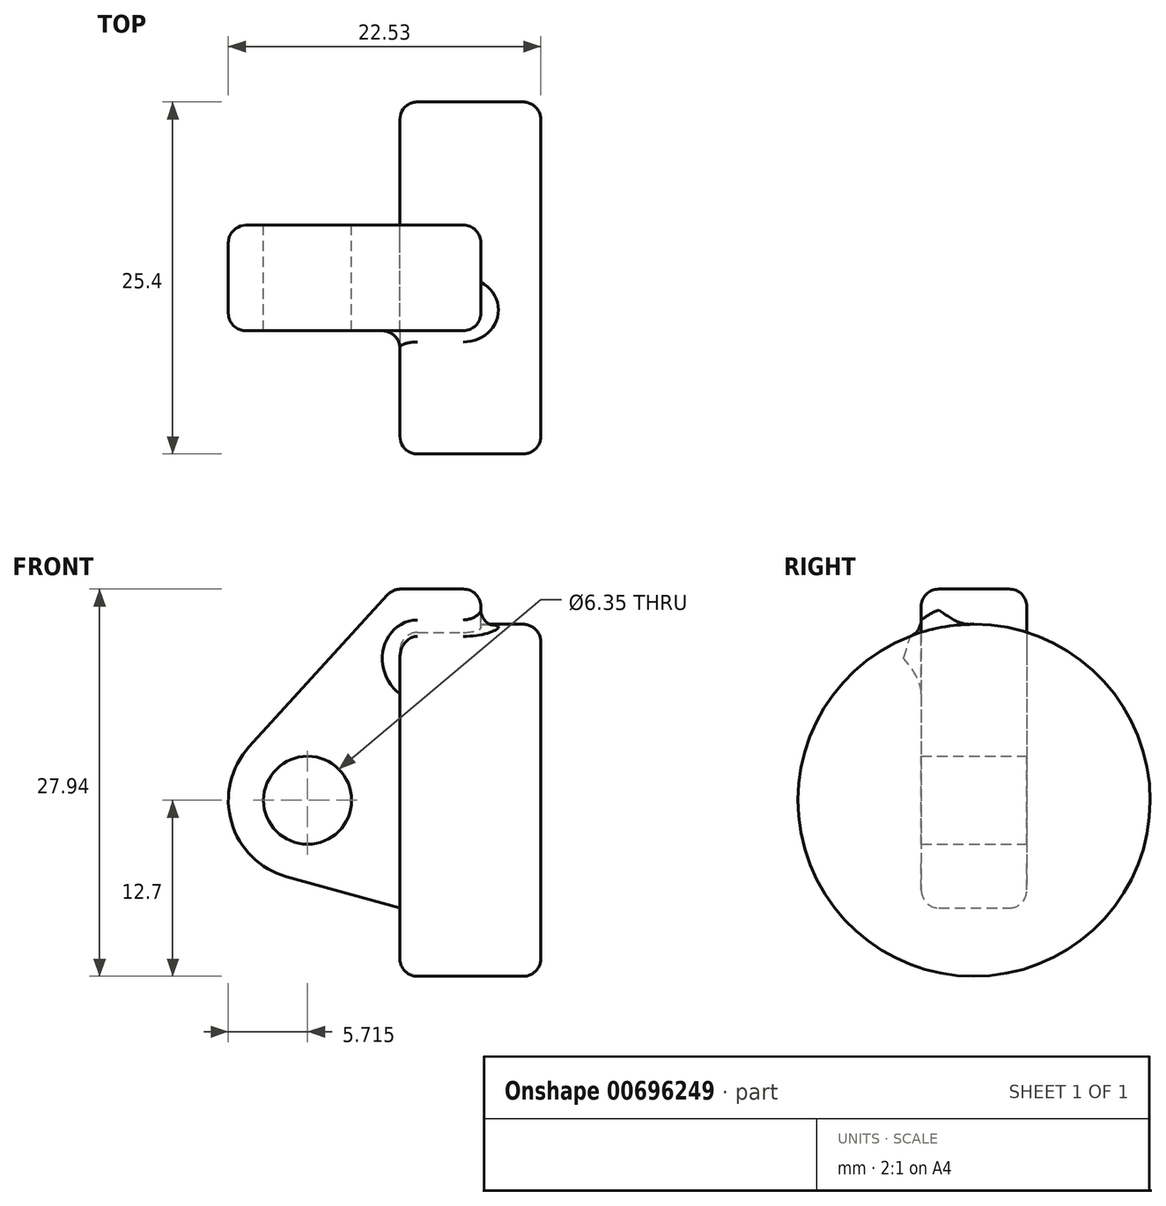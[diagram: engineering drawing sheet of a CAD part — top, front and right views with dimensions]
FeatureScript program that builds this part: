
annotation { "Feature Type Name" : "Feature", "Feature Type Description" : "" }
export const myFeature = defineFeature(function(context is Context, id is Id, definition is map)
    precondition{}
    {
        {
            var Q0;
            Q0=qCreatedBy(makeId("Front.planeOp"),FACE);
            var sketch = newSketch(context, id + "F0", { "sketchPlane" : qUnion([Q0])});
            skLineSegment(sketch, "E0", {"start": v(0, 0) * mm, "end": v(0, 12.7) * mm});
            skLineSegment(sketch, "E1", {"start": v(0, 12.7) * mm, "end": v(10.16, 12.7) * mm});
            skLineSegment(sketch, "E2", {"start": v(10.16, 12.7) * mm, "end": v(10.16, 10.16) * mm});
            skLineSegment(sketch, "E3", {"start": v(10.16, 10.16) * mm, "end": v(56.13, 10.16) * mm});
            skLineSegment(sketch, "E4", {"start": v(56.13, 10.16) * mm, "end": v(56.13, 12.7) * mm});
            skLineSegment(sketch, "E5", {"start": v(56.13, 12.7) * mm, "end": v(66.3, 12.7) * mm});
            skLineSegment(sketch, "E6", {"start": v(66.3, 12.7) * mm, "end": v(66.3, 0) * mm});
            skLineSegment(sketch, "E7", {"start": v(66.3, 0) * mm, "end": v(0, 0) * mm});
            skLineSegment(sketch, "E8", {"start": v(5.84, 15.24) * mm, "end": v(-0.5, 15.24) * mm});
            skLineSegment(sketch, "E9", {"start": v(-0.5, 15.24) * mm, "end": v(-10.88, 3.85) * mm});
            skLineSegment(sketch, "E10", {"start": v(0, 0) * mm, "end": v(-6.65, 0) * mm});
            skCircle(sketch, "E11", {"center": v(-6.65, 0) * mm, "radius": 5.72 * mm});
            skCircle(sketch, "E12", {"center": v(-6.65, 0) * mm, "radius": 3.18 * mm});
            skLineSegment(sketch, "E13", {"start": v(5.84, 15.24) * mm, "end": v(5.84, -9.4) * mm});
            skLineSegment(sketch, "E14", {"start": v(5.84, -9.4) * mm, "end": v(-8.18, -5.5) * mm});
            skLineSegment(sketch, "E15", {"start": v(0, 0) * mm, "end": v(0, -7.78) * mm});
            skSolve(sketch);
        }
        {
            var Q0;
            {var subQ0=sQuery(id+"F0.wireOp",EDGE,"E2");Q0=makeQuery(id+"F0.imprint","IMPRINT",FACE,{"disambiguationData":[TD([[makeQuery(id+"F0.imprint","IMPRINT",EDGE,{"derivedFrom":subQ0}),-1.0]])]});}
            var Q1;
            {var subQ0=sQuery(id+"F0.wireOp",EDGE,"E0");Q1=makeQuery(id+"F0.imprint","IMPRINT",FACE,{"disambiguationData":[TD([[makeQuery(id+"F0.imprint","IMPRINT",EDGE,{"derivedFrom":subQ0}),-1.0]])]});}
            var Q2;
            Q2=sQuery(id+"F0.wireOp",EDGE,"E7");
            revolve(context, id + "F1", {"entities" : qUnion([Q0, Q1]), "axis" : qUnion([Q2]), "revolveType" : RevolveType.FULL});
        }
        {
            var Q0;
            {var subQ1=sQuery(id+"F0.wireOp",EDGE,"E0");Q0=makeQuery(id+"F0.imprint","IMPRINT",FACE,{"disambiguationData":[TD([[makeQuery(id+"F0.imprint","IMPRINT",EDGE,{"derivedFrom":subQ1}),1.0]])]});}
            var Q1;
            {var subQ5=sQuery(id+"F0.wireOp",EDGE,"E12");Q1=makeQuery(id+"F0.imprint","IMPRINT",FACE,{"disambiguationData":[TD([[makeQuery(id+"F0.imprint","IMPRINT",EDGE,{"derivedFrom":subQ5}),-1.0]])]});}
            var Q2;
            {var subQ0=sQuery(id+"F0.wireOp",EDGE,"E15");Q2=makeQuery(id+"F0.imprint","IMPRINT",FACE,{"disambiguationData":[TD([[makeQuery(id+"F0.imprint","IMPRINT",EDGE,{"derivedFrom":subQ0}),-1.0]])]});}
            var Q3;
            {var subQ0=sQuery(id+"F0.wireOp",EDGE,"E0");Q3=makeQuery(id+"F0.imprint","IMPRINT",FACE,{"disambiguationData":[TD([[makeQuery(id+"F0.imprint","IMPRINT",EDGE,{"derivedFrom":subQ0}),-1.0]])]});}
            var Q4;
            {var subQ0=sQuery(id+"F0.wireOp",EDGE,"E15");Q4=makeQuery(id+"F0.imprint","IMPRINT",FACE,{"disambiguationData":[TD([[makeQuery(id+"F0.imprint","IMPRINT",EDGE,{"derivedFrom":subQ0}),1.0]])]});}
            extrude(context, id + "F2", {"entities" : qUnion([Q0, Q1, Q2, Q3, Q4]), "operationType" : NewBodyOperationType.ADD, "endBound" : BoundingType.SYMMETRIC, "depth" : 7.62 * mm, "offsetDistance" : 25.4 * mm});
        }
        {
            var Q0;
            Q0=makeQuery(id+"F3.boolean.opBoolean","SPLIT",FACE,{"disambiguationData":[TD([makeQuery(id+"F3.opExtrude","SWEPT_FACE",FACE,{"disambiguationData":[OSD([sQuery(id+"FeWnoBpIE6AIeDr_1.wireOp",EDGE,"sYwXt4bQ-ehGj-KG2p-6Kim-FAGufsxMGpLw")])]})])],"derivedFrom":makeQuery(id+"F1.opRevolve","SWEPT_FACE",FACE,{"disambiguationData":[OSD([sQuery(id+"F0.wireOp",EDGE,"E6")])]})});
            var Q1;
            Q1=makeQuery(id+"F1.opRevolve","SWEPT_FACE",FACE,{"disambiguationData":[OSD([sQuery(id+"F0.wireOp",EDGE,"E2")])]});
            extrude(context, id + "F5", {"entities" : qUnion([Q0]), "operationType" : NewBodyOperationType.REMOVE, "endBound" : BoundingType.UP_TO_SURFACE, "oppositeDirection" : true, "depth" : 25.4 * mm, "endBoundEntityFace" : qUnion([Q1]), "offsetDistance" : 25.4 * mm});
        }
        {
            var Q0;
            {var subQ0=sQuery(id+"F0.wireOp",EDGE,"E5");var subQ1=sQuery(id+"F0.wireOp",EDGE,"E6");Q0=makeQuery(id+"F3.boolean.opBoolean","SPLIT",EDGE,{"disambiguationData":[topologyDisambiguationEdgeConnected([makeQuery(id+"F1.opRevolve","SWEPT_FACE",FACE,{"disambiguationData":[OSD([subQ1])]})])],"derivedFrom":makeQuery(id+"F1.opRevolve","SWEPT_EDGE",EDGE,{"disambiguationData":[OSD([subQ0,subQ1])]})});}
            var Q1;
            Q1=makeQuery(id+"F1.opRevolve","SWEPT_EDGE",EDGE,{"disambiguationData":[OSD([sQuery(id+"F0.wireOp",EDGE,"E4"),sQuery(id+"F0.wireOp",EDGE,"E5")])]});
            var Q2;
            Q2=makeQuery(id+"F3.opExtrude","SWEPT_FACE",FACE,{"disambiguationData":[OSD([sQuery(id+"FeWnoBpIE6AIeDr_1.wireOp",EDGE,"koyzqUWy-vNv5-K2rH-FPf9-U3UE0hhaecZR")])]});
            var Q3;
            {var subQ0=sQuery(id+"FeWnoBpIE6AIeDr_1.wireOp",EDGE,"JIyT0qjO-2QI5-vtE6-71wE-rBa4ktSNC4SN");var subQ1=sQuery(id+"FeWnoBpIE6AIeDr_1.wireOp",EDGE,"dYmv9FUA-QIOy-5e5U-vTmS-nWUvyouI4BtE");Q3=makeQuery(id+"F4.boolean.opBoolean","MERGE",EDGE,{"derivedFrom":[makeQuery(id+"F3.opExtrude","SWEPT_EDGE",EDGE,{"disambiguationData":[OSD([subQ1,subQ0])]}),makeQuery(id+"F4.opExtrude","SWEPT_EDGE",EDGE,{"disambiguationData":[OSD([subQ1,subQ0])]})]});}
            var Q4;
            {var subQ0=sQuery(id+"FeWnoBpIE6AIeDr_1.wireOp",EDGE,"JIyT0qjO-2QI5-vtE6-71wE-rBa4ktSNC4SN");var subQ1=sQuery(id+"FeWnoBpIE6AIeDr_1.wireOp",EDGE,"dKOQ6eiB-urNR-Gqhq-Mxef-VnIKHvAkL9Sr");Q4=makeQuery(id+"F4.boolean.opBoolean","MERGE",EDGE,{"derivedFrom":[makeQuery(id+"F3.opExtrude","SWEPT_EDGE",EDGE,{"disambiguationData":[OSD([subQ1,subQ0])]}),makeQuery(id+"F4.opExtrude","SWEPT_EDGE",EDGE,{"disambiguationData":[OSD([subQ1,subQ0])]})]});}
            var Q5;
            Q5=makeQuery(id+"F3.opExtrude","CAP_EDGE",EDGE,{"disambiguationData":[OSD([sQuery(id+"FeWnoBpIE6AIeDr_1.wireOp",EDGE,"JIyT0qjO-2QI5-vtE6-71wE-rBa4ktSNC4SN")])],"isStart":false});
            var Q6;
            Q6=makeQuery(id+"F4.opExtrude","CAP_EDGE",EDGE,{"disambiguationData":[OSD([sQuery(id+"FeWnoBpIE6AIeDr_1.wireOp",EDGE,"JIyT0qjO-2QI5-vtE6-71wE-rBa4ktSNC4SN")])],"isStart":false});
            var Q7;
            Q7=makeQuery(id+"F4.opExtrude","CAP_EDGE",EDGE,{"disambiguationData":[OSD([sQuery(id+"FeWnoBpIE6AIeDr_1.wireOp",EDGE,"dKOQ6eiB-urNR-Gqhq-Mxef-VnIKHvAkL9Sr")])],"isStart":false});
            var Q8;
            Q8=makeQuery(id+"F1.opRevolve","SWEPT_EDGE",EDGE,{"disambiguationData":[OSD([sQuery(id+"F0.wireOp",EDGE,"E1"),sQuery(id+"F0.wireOp",EDGE,"E2")])]});
            var Q9;
            Q9=makeQuery(id+"F1.opRevolve","SWEPT_EDGE",EDGE,{"disambiguationData":[OSD([sQuery(id+"F0.wireOp",EDGE,"E0"),sQuery(id+"F0.wireOp",EDGE,"E1")])]});
            var Q10;
            Q10=makeQuery(id+"F2.opExtrude","SWEPT_FACE",FACE,{"disambiguationData":[OSD([sQuery(id+"F0.wireOp",EDGE,"E9")])]});
            var Q11;
            Q11=makeQuery(id+"F2.opExtrude","CAP_EDGE",EDGE,{"disambiguationData":[OSD([sQuery(id+"F0.wireOp",EDGE,"E8")])],"isStart":true});
            var Q12;
            Q12=makeQuery(id+"F2.opExtrude","SWEPT_EDGE",EDGE,{"disambiguationData":[OSD([sQuery(id+"F0.wireOp",EDGE,"E8"),sQuery(id+"F0.wireOp",EDGE,"E13")])]});
            var Q13;
            Q13=makeQuery(id+"F2.opExtrude","CAP_EDGE",EDGE,{"disambiguationData":[OSD([sQuery(id+"F0.wireOp",EDGE,"E8")])],"isStart":false});
            var Q14;
            Q14=makeQuery(id+"F2.opExtrude","CAP_EDGE",EDGE,{"disambiguationData":[OSD([sQuery(id+"F0.wireOp",EDGE,"E13")])],"isStart":false});
            var Q15;
            Q15=makeQuery(id+"F2.opExtrude","CAP_EDGE",EDGE,{"disambiguationData":[OSD([sQuery(id+"F0.wireOp",EDGE,"E13")])],"isStart":true});
            var Q16;
            Q16=makeQuery(id+"F2.opExtrude","CAP_EDGE",EDGE,{"disambiguationData":[OSD([sQuery(id+"F0.wireOp",EDGE,"E0"),sQuery(id+"F0.wireOp",EDGE,"E15")])],"isStart":true});
            var Q17;
            Q17=makeQuery(id+"F2.opExtrude","CAP_EDGE",EDGE,{"disambiguationData":[OSD([sQuery(id+"F0.wireOp",EDGE,"E0"),sQuery(id+"F0.wireOp",EDGE,"E15")])],"isStart":false});
            var Q18;
            Q18=makeQuery(id+"F2.opExtrude","CAP_EDGE",EDGE,{"disambiguationData":[OSD([sQuery(id+"F0.wireOp",EDGE,"E1")])],"isStart":false});
            var Q19;
            Q19=makeQuery(id+"F2.opExtrude","CAP_EDGE",EDGE,{"disambiguationData":[OSD([sQuery(id+"F0.wireOp",EDGE,"E1")])],"isStart":true});
            var Q20;
            Q20=makeQuery(id+"F2.boolean.opBoolean","INTERSECT",EDGE,{"derivedFrom":[makeQuery(id+"F1.opRevolve","SWEPT_FACE",FACE,{"disambiguationData":[OSD([sQuery(id+"F0.wireOp",EDGE,"E1")])]}),makeQuery(id+"F2.opExtrude","CAP_FACE",FACE,{"disambiguationData":[OSD([sQuery(id+"F0.wireOp",EDGE,"E8"),sQuery(id+"F0.wireOp",EDGE,"E9"),sQuery(id+"F0.wireOp",EDGE,"E11"),sQuery(id+"F0.wireOp",EDGE,"E12"),sQuery(id+"F0.wireOp",EDGE,"E13"),sQuery(id+"F0.wireOp",EDGE,"E14")])],"isStart":false})]});
            fillet(context, id + "F7", {"entities" : qUnion([Q0, Q1, Q2, Q3, Q4, Q5, Q6, Q7, Q8, Q9, Q10, Q11, Q12, Q13, Q14, Q15, Q16, Q17, Q18, Q19, Q20]), "radius" : 1.27 * mm, "tangentPropagation" : true, "allowEdgeOverflow" : false});
        }
    });
